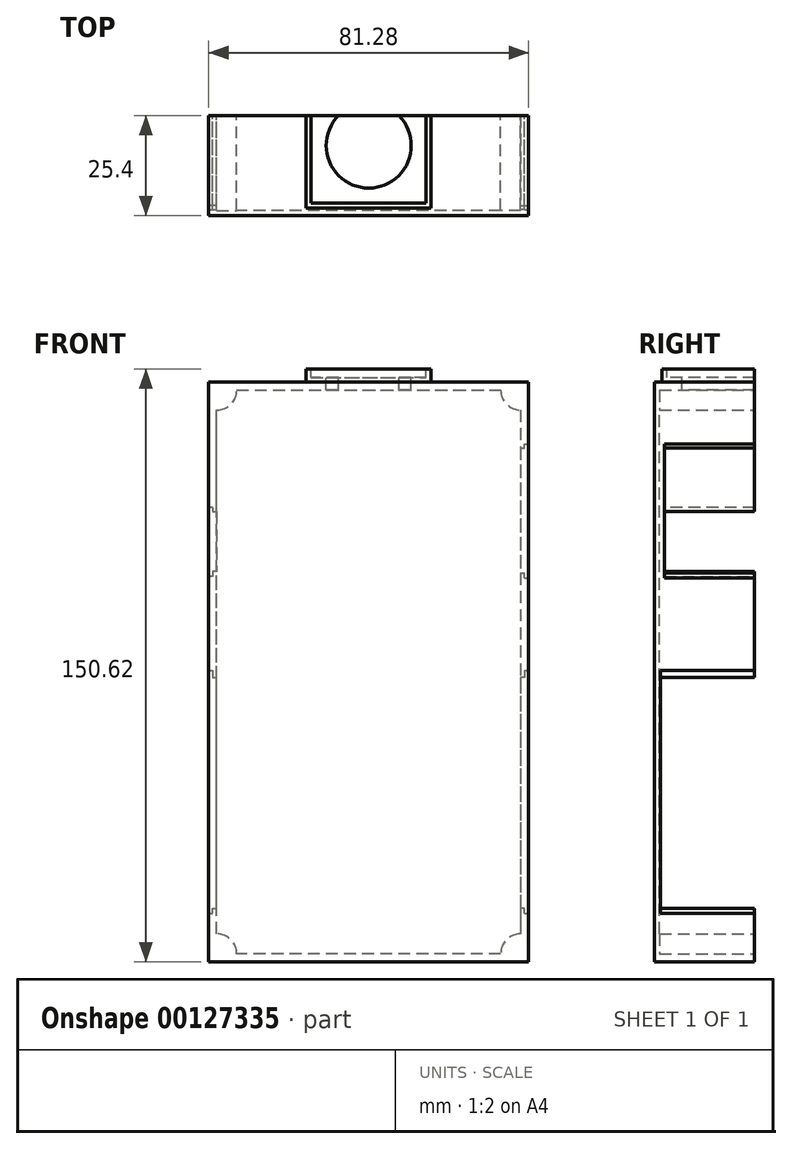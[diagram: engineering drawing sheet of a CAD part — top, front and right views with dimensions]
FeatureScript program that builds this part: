
annotation { "Feature Type Name" : "Feature", "Feature Type Description" : "" }
export const myFeature = defineFeature(function(context is Context, id is Id, definition is map)
    precondition{}
    {
        {
            var Q0;
            Q0=qCreatedBy(makeId("Front.planeOp"),FACE);
            var sketch = newSketch(context, id + "F0", { "sketchPlane" : qUnion([Q0])});
            skLineSegment(sketch, "E0", {"start": v(36.47, 73.76) * mm, "end": v(-44.81, 73.76) * mm});
            skLineSegment(sketch, "E1", {"start": v(-44.81, 73.76) * mm, "end": v(-44.81, -40.54) * mm});
            skLineSegment(sketch, "E2", {"start": v(36.47, -40.54) * mm, "end": v(36.47, 73.76) * mm});
            skLineSegment(sketch, "E3", {"start": v(36.47, -40.54) * mm, "end": v(36.47, -73.56) * mm});
            skLineSegment(sketch, "E4", {"start": v(36.47, -73.56) * mm, "end": v(-44.81, -73.56) * mm});
            skLineSegment(sketch, "E5", {"start": v(-44.81, -73.56) * mm, "end": v(-44.81, -40.54) * mm});
            skSolve(sketch);
        }
        {
            var Q0;
            Q0 = qSketchRegion(id + "F0", true);
            extrude(context, id + "F1", {"entities" : qUnion([Q0]), "depth" : 25.4 * mm});
        }
        {
            var Q0;
            Q0=makeQuery(id+"F1.opExtrude","CAP_FACE",FACE,{"disambiguationData":[OSD([sQuery(id+"F0.wireOp",EDGE,"E0"),sQuery(id+"F0.wireOp",EDGE,"E1"),sQuery(id+"F0.wireOp",EDGE,"9LGxaBVT-J4aD-Pj7p-0tie-yeeoXnwk5BCI"),sQuery(id+"F0.wireOp",EDGE,"E2")])],"isStart":true});
            var sketch = newSketch(context, id + "F2", { "sketchPlane" : qUnion([Q0])});
            skLineSegment(sketch, "E6", {"start": v(-34.44, 71.73) * mm, "end": v(-34.44, -71.53) * mm});
            skLineSegment(sketch, "E7", {"start": v(-34.44, -71.53) * mm, "end": v(42.78, -71.53) * mm});
            skLineSegment(sketch, "E8", {"start": v(42.78, -71.53) * mm, "end": v(42.78, 71.73) * mm});
            skLineSegment(sketch, "E9", {"start": v(42.78, 71.73) * mm, "end": v(-34.44, 71.73) * mm});
            skSolve(sketch);
        }
        {
            var Q0;
            Q0 = qSketchRegion(id + "F2", true);
            extrude(context, id + "F3", {"entities" : qUnion([Q0]), "operationType" : NewBodyOperationType.REMOVE, "oppositeDirection" : true, "depth" : 24.13 * mm});
        }
        {
            var Q0;
            Q0=makeQuery(id+"F1.opExtrude","SWEPT_FACE",FACE,{"disambiguationData":[OSD([sQuery(id+"F0.wireOp",EDGE,"E2")])]});
            var sketch = newSketch(context, id + "F4", { "sketchPlane" : qUnion([Q0])});
            skLineSegment(sketch, "E10", {"start": v(-25.4, 20.55) * mm, "end": v(-25.4, -0.03) * mm});
            skLineSegment(sketch, "E11", {"start": v(-13.14, -8) * mm, "end": v(-13.14, -14.85) * mm});
            skLineSegment(sketch, "E12", {"start": v(-13.14, -14.85) * mm, "end": v(-12.26, -14.85) * mm});
            skLineSegment(sketch, "E13", {"start": v(-12.26, -14.85) * mm, "end": v(-12.26, -8) * mm});
            skLineSegment(sketch, "E14", {"start": v(-12.26, -8) * mm, "end": v(-13.14, -8) * mm});
            skLineSegment(sketch, "E15", {"start": v(-16.13, -19.42) * mm, "end": v(-16.13, -20.31) * mm});
            skLineSegment(sketch, "E16", {"start": v(-16.13, -20.31) * mm, "end": v(-9.27, -20.31) * mm});
            skLineSegment(sketch, "E17", {"start": v(-9.27, -20.31) * mm, "end": v(-9.27, -19.42) * mm});
            skLineSegment(sketch, "E18", {"start": v(-9.27, -19.42) * mm, "end": v(-16.13, -19.42) * mm});
            skLineSegment(sketch, "E19", {"start": v(-16.13, -27.42) * mm, "end": v(-16.13, -28.31) * mm});
            skLineSegment(sketch, "E20", {"start": v(-16.13, -28.31) * mm, "end": v(-9.27, -28.31) * mm});
            skLineSegment(sketch, "E21", {"start": v(-9.27, -28.31) * mm, "end": v(-9.27, -27.42) * mm});
            skLineSegment(sketch, "E22", {"start": v(-9.27, -27.42) * mm, "end": v(-16.13, -27.42) * mm});
            skLineSegment(sketch, "E23", {"start": v(-21.46, -16.06) * mm, "end": v(-21.46, -22.91) * mm});
            skLineSegment(sketch, "E24", {"start": v(-21.46, -22.91) * mm, "end": v(-20.57, -22.91) * mm});
            skLineSegment(sketch, "E25", {"start": v(-20.57, -22.91) * mm, "end": v(-20.57, -16.06) * mm});
            skLineSegment(sketch, "E26", {"start": v(-20.57, -16.06) * mm, "end": v(-21.46, -16.06) * mm});
            skLineSegment(sketch, "E27", {"start": v(-4.83, -16.06) * mm, "end": v(-4.83, -22.91) * mm});
            skLineSegment(sketch, "E28", {"start": v(-4.83, -22.91) * mm, "end": v(-3.94, -22.91) * mm});
            skLineSegment(sketch, "E29", {"start": v(-3.94, -22.91) * mm, "end": v(-3.94, -16.06) * mm});
            skLineSegment(sketch, "E30", {"start": v(-3.94, -16.06) * mm, "end": v(-4.83, -16.06) * mm});
            skSolve(sketch);
        }
        {
            var Q0;
            Q0 = qSketchRegion(id + "F4", true);
            extrude(context, id + "F5", {"entities" : qUnion([Q0]), "operationType" : NewBodyOperationType.REMOVE, "endBound" : BoundingType.THROUGH_ALL, "oppositeDirection" : true, "depth" : 25.4 * mm});
        }
        {
            var Q0;
            Q0=makeQuery(id+"F1.opExtrude","SWEPT_FACE",FACE,{"disambiguationData":[OSD([sQuery(id+"F0.wireOp",EDGE,"E2")])]});
            var sketch = newSketch(context, id + "F6", { "sketchPlane" : qUnion([Q0])});
            skLineSegment(sketch, "E31", {"start": v(-25.4, 20.55) * mm, "end": v(-25.4, -0.03) * mm});
            skLineSegment(sketch, "E32", {"start": v(-19.94, 28.85) * mm, "end": v(-19.94, 28.17) * mm});
            skLineSegment(sketch, "E33", {"start": v(-19.94, 28.17) * mm, "end": v(-14.94, 28.17) * mm});
            skLineSegment(sketch, "E34", {"start": v(-14.94, 28.17) * mm, "end": v(-14.94, 28.85) * mm});
            skLineSegment(sketch, "E35", {"start": v(-14.94, 28.85) * mm, "end": v(-19.94, 28.85) * mm});
            skLineSegment(sketch, "E36", {"start": v(-10.46, 28.85) * mm, "end": v(-5.46, 28.85) * mm});
            skLineSegment(sketch, "E37", {"start": v(-5.46, 28.85) * mm, "end": v(-5.46, 28.17) * mm});
            skLineSegment(sketch, "E38", {"start": v(-5.46, 28.17) * mm, "end": v(-10.46, 28.17) * mm});
            skLineSegment(sketch, "E39", {"start": v(-10.46, 28.17) * mm, "end": v(-10.46, 28.85) * mm});
            skLineSegment(sketch, "E40", {"start": v(-19.94, 37.16) * mm, "end": v(-19.94, 36.47) * mm});
            skLineSegment(sketch, "E41", {"start": v(-19.94, 36.47) * mm, "end": v(-14.94, 36.47) * mm});
            skLineSegment(sketch, "E42", {"start": v(-14.94, 36.47) * mm, "end": v(-14.94, 37.16) * mm});
            skLineSegment(sketch, "E43", {"start": v(-14.94, 37.16) * mm, "end": v(-19.94, 37.16) * mm});
            skLineSegment(sketch, "E44", {"start": v(-10.46, 37.16) * mm, "end": v(-10.46, 36.47) * mm});
            skLineSegment(sketch, "E45", {"start": v(-10.46, 36.47) * mm, "end": v(-5.46, 36.47) * mm});
            skLineSegment(sketch, "E46", {"start": v(-5.46, 36.47) * mm, "end": v(-5.46, 37.16) * mm});
            skLineSegment(sketch, "E47", {"start": v(-5.46, 37.16) * mm, "end": v(-10.46, 37.16) * mm});
            skLineSegment(sketch, "E48", {"start": v(-19.94, 45.46) * mm, "end": v(-19.94, 44.78) * mm});
            skLineSegment(sketch, "E49", {"start": v(-19.94, 44.78) * mm, "end": v(-14.94, 44.78) * mm});
            skLineSegment(sketch, "E50", {"start": v(-14.94, 44.78) * mm, "end": v(-14.94, 45.46) * mm});
            skLineSegment(sketch, "E51", {"start": v(-14.94, 45.46) * mm, "end": v(-19.94, 45.46) * mm});
            skLineSegment(sketch, "E52", {"start": v(-10.46, 45.46) * mm, "end": v(-10.46, 44.78) * mm});
            skLineSegment(sketch, "E53", {"start": v(-10.46, 44.78) * mm, "end": v(-5.46, 44.78) * mm});
            skLineSegment(sketch, "E54", {"start": v(-5.46, 44.78) * mm, "end": v(-5.46, 45.46) * mm});
            skLineSegment(sketch, "E55", {"start": v(-5.46, 45.46) * mm, "end": v(-10.46, 45.46) * mm});
            skLineSegment(sketch, "E56", {"start": v(-19.94, 53.77) * mm, "end": v(-19.94, 53.08) * mm});
            skLineSegment(sketch, "E57", {"start": v(-19.94, 53.08) * mm, "end": v(-14.94, 53.08) * mm});
            skLineSegment(sketch, "E58", {"start": v(-14.94, 53.08) * mm, "end": v(-14.94, 53.77) * mm});
            skLineSegment(sketch, "E59", {"start": v(-14.94, 53.77) * mm, "end": v(-19.94, 53.77) * mm});
            skLineSegment(sketch, "E60", {"start": v(-10.46, 53.77) * mm, "end": v(-10.46, 53.08) * mm});
            skLineSegment(sketch, "E61", {"start": v(-10.46, 53.08) * mm, "end": v(-5.46, 53.08) * mm});
            skLineSegment(sketch, "E62", {"start": v(-5.46, 53.08) * mm, "end": v(-5.46, 53.77) * mm});
            skLineSegment(sketch, "E63", {"start": v(-5.46, 53.77) * mm, "end": v(-10.46, 53.77) * mm});
            skSolve(sketch);
        }
        {
            var Q0;
            Q0 = qSketchRegion(id + "F6", true);
            extrude(context, id + "F7", {"entities" : qUnion([Q0]), "operationType" : NewBodyOperationType.REMOVE, "endBound" : BoundingType.THROUGH_ALL, "oppositeDirection" : true, "depth" : 25.4 * mm});
        }
        {
            var Q0;
            Q0=makeQuery(id+"F1.opExtrude","SWEPT_FACE",FACE,{"disambiguationData":[OSD([sQuery(id+"F0.wireOp",EDGE,"E1")])]});
            var sketch = newSketch(context, id + "F8", { "sketchPlane" : qUnion([Q0])});
            skLineSegment(sketch, "E64", {"start": v(5.46, 53.77) * mm, "end": v(5.46, 53.08) * mm});
            skLineSegment(sketch, "E65", {"start": v(5.46, 53.08) * mm, "end": v(10.46, 53.08) * mm});
            skLineSegment(sketch, "E66", {"start": v(10.46, 53.08) * mm, "end": v(10.46, 53.77) * mm});
            skLineSegment(sketch, "E67", {"start": v(10.46, 53.77) * mm, "end": v(5.46, 53.77) * mm});
            skLineSegment(sketch, "E68", {"start": v(14.94, 53.77) * mm, "end": v(14.94, 53.08) * mm});
            skLineSegment(sketch, "E69", {"start": v(14.94, 53.08) * mm, "end": v(19.94, 53.08) * mm});
            skLineSegment(sketch, "E70", {"start": v(19.94, 53.08) * mm, "end": v(19.94, 53.77) * mm});
            skLineSegment(sketch, "E71", {"start": v(19.94, 53.77) * mm, "end": v(14.94, 53.77) * mm});
            skLineSegment(sketch, "E72", {"start": v(5.46, 45.46) * mm, "end": v(5.46, 44.78) * mm});
            skLineSegment(sketch, "E73", {"start": v(5.46, 44.78) * mm, "end": v(10.46, 44.78) * mm});
            skLineSegment(sketch, "E74", {"start": v(10.46, 44.78) * mm, "end": v(10.46, 45.46) * mm});
            skLineSegment(sketch, "E75", {"start": v(10.46, 45.46) * mm, "end": v(5.46, 45.46) * mm});
            skLineSegment(sketch, "E76", {"start": v(14.94, 45.46) * mm, "end": v(14.94, 44.78) * mm});
            skLineSegment(sketch, "E77", {"start": v(14.94, 44.78) * mm, "end": v(19.94, 44.78) * mm});
            skLineSegment(sketch, "E78", {"start": v(19.94, 44.78) * mm, "end": v(19.94, 45.46) * mm});
            skLineSegment(sketch, "E79", {"start": v(19.94, 45.46) * mm, "end": v(14.94, 45.46) * mm});
            skSolve(sketch);
        }
        {
            var Q0;
            Q0 = qSketchRegion(id + "F8", true);
            extrude(context, id + "F9", {"entities" : qUnion([Q0]), "operationType" : NewBodyOperationType.ADD, "oppositeDirection" : true, "depth" : 2.03 * mm});
        }
        {
            var Q0;
            Q0=makeQuery(id+"F1.opExtrude","SWEPT_FACE",FACE,{"disambiguationData":[OSD([sQuery(id+"F0.wireOp",EDGE,"E2")])]});
            var sketch = newSketch(context, id + "F10", { "sketchPlane" : qUnion([Q0])});
            skLineSegment(sketch, "E80", {"start": v(-19.43, -15.67) * mm, "end": v(-22.6, -15.67) * mm});
            skLineSegment(sketch, "E81", {"start": v(-22.6, -15.67) * mm, "end": v(-22.6, -23.3) * mm});
            skLineSegment(sketch, "E82", {"start": v(-22.6, -23.3) * mm, "end": v(-19.43, -23.3) * mm});
            skLineSegment(sketch, "E83", {"start": v(-19.43, -23.3) * mm, "end": v(-19.43, -15.67) * mm});
            skLineSegment(sketch, "E84", {"start": v(-16.51, -18.28) * mm, "end": v(-16.51, -21.45) * mm});
            skLineSegment(sketch, "E85", {"start": v(-16.51, -21.45) * mm, "end": v(-8.9, -21.45) * mm});
            skLineSegment(sketch, "E86", {"start": v(-8.9, -21.45) * mm, "end": v(-8.9, -18.28) * mm});
            skLineSegment(sketch, "E87", {"start": v(-8.9, -18.28) * mm, "end": v(-16.51, -18.28) * mm});
            skLineSegment(sketch, "E88", {"start": v(-2.8, -15.67) * mm, "end": v(-5.97, -15.67) * mm});
            skLineSegment(sketch, "E89", {"start": v(-5.97, -15.67) * mm, "end": v(-5.97, -23.3) * mm});
            skLineSegment(sketch, "E90", {"start": v(-5.97, -23.3) * mm, "end": v(-2.8, -23.3) * mm});
            skLineSegment(sketch, "E91", {"start": v(-2.8, -23.3) * mm, "end": v(-2.8, -15.67) * mm});
            skLineSegment(sketch, "E92", {"start": v(-11.11, -7.61) * mm, "end": v(-14.29, -7.61) * mm});
            skLineSegment(sketch, "E93", {"start": v(-14.29, -7.61) * mm, "end": v(-14.29, -15.23) * mm});
            skLineSegment(sketch, "E94", {"start": v(-14.29, -15.23) * mm, "end": v(-11.11, -15.23) * mm});
            skLineSegment(sketch, "E95", {"start": v(-11.11, -15.23) * mm, "end": v(-11.11, -7.61) * mm});
            skLineSegment(sketch, "E96", {"start": v(-16.5, -26.28) * mm, "end": v(-16.5, -29.45) * mm});
            skLineSegment(sketch, "E97", {"start": v(-16.5, -29.45) * mm, "end": v(-8.89, -29.45) * mm});
            skLineSegment(sketch, "E98", {"start": v(-8.89, -29.45) * mm, "end": v(-8.89, -26.28) * mm});
            skLineSegment(sketch, "E99", {"start": v(-8.89, -26.28) * mm, "end": v(-16.5, -26.28) * mm});
            skLineSegment(sketch, "E100", {"start": v(-10.1, -6.6) * mm, "end": v(-15.3, -6.6) * mm});
            skLineSegment(sketch, "E101", {"start": v(-15.3, -6.6) * mm, "end": v(-15.3, -16.25) * mm});
            skLineSegment(sketch, "E102", {"start": v(-15.3, -16.25) * mm, "end": v(-10.1, -16.25) * mm});
            skLineSegment(sketch, "E103", {"start": v(-10.1, -16.25) * mm, "end": v(-10.1, -6.6) * mm});
            skLineSegment(sketch, "E104", {"start": v(-23.62, -14.66) * mm, "end": v(-23.62, -24.31) * mm});
            skLineSegment(sketch, "E105", {"start": v(-23.62, -24.31) * mm, "end": v(-18.41, -24.31) * mm});
            skLineSegment(sketch, "E106", {"start": v(-18.42, -24.31) * mm, "end": v(-18.42, -14.66) * mm});
            skLineSegment(sketch, "E107", {"start": v(-18.42, -14.66) * mm, "end": v(-23.62, -14.66) * mm});
            skLineSegment(sketch, "E108", {"start": v(-1.78, -14.66) * mm, "end": v(-6.98, -14.66) * mm});
            skLineSegment(sketch, "E109", {"start": v(-6.98, -14.66) * mm, "end": v(-6.98, -24.31) * mm});
            skLineSegment(sketch, "E110", {"start": v(-6.98, -24.31) * mm, "end": v(-1.78, -24.31) * mm});
            skLineSegment(sketch, "E111", {"start": v(-1.78, -24.31) * mm, "end": v(-1.78, -14.66) * mm});
            skLineSegment(sketch, "E112", {"start": v(-17.53, -17.26) * mm, "end": v(-17.53, -22.47) * mm});
            skLineSegment(sketch, "E113", {"start": v(-17.53, -22.47) * mm, "end": v(-7.87, -22.47) * mm});
            skLineSegment(sketch, "E114", {"start": v(-7.87, -22.47) * mm, "end": v(-7.87, -17.26) * mm});
            skLineSegment(sketch, "E115", {"start": v(-7.87, -17.26) * mm, "end": v(-17.53, -17.26) * mm});
            skLineSegment(sketch, "E116", {"start": v(-17.53, -25.26) * mm, "end": v(-17.53, -30.47) * mm});
            skLineSegment(sketch, "E117", {"start": v(-17.53, -30.47) * mm, "end": v(-8.25, -30.47) * mm});
            skLineSegment(sketch, "E118", {"start": v(-8.25, -30.47) * mm, "end": v(-8.25, -25.26) * mm});
            skLineSegment(sketch, "E119", {"start": v(-8.25, -25.26) * mm, "end": v(-17.53, -25.26) * mm});
            skSolve(sketch);
        }
        {
            var Q0;
            Q0 = qSketchRegion(id + "F10", true);
            extrude(context, id + "F11", {"entities" : qUnion([Q0]), "operationType" : NewBodyOperationType.ADD, "oppositeDirection" : true, "depth" : 12.95 * mm});
        }
        {
            var Q0;
            Q0=makeQuery(id+"F1.opExtrude","SWEPT_FACE",FACE,{"disambiguationData":[OSD([sQuery(id+"F0.wireOp",EDGE,"E2")])]});
            var sketch = newSketch(context, id + "F12", { "sketchPlane" : qUnion([Q0])});
            skLineSegment(sketch, "E120", {"start": v(-21.25, 30.1) * mm, "end": v(-21.25, 26.92) * mm});
            skLineSegment(sketch, "E121", {"start": v(-21.25, 26.92) * mm, "end": v(-13.63, 26.92) * mm});
            skLineSegment(sketch, "E122", {"start": v(-13.63, 26.92) * mm, "end": v(-13.63, 30.1) * mm});
            skLineSegment(sketch, "E123", {"start": v(-13.63, 30.1) * mm, "end": v(-21.25, 30.1) * mm});
            skLineSegment(sketch, "E124", {"start": v(-22, 30.86) * mm, "end": v(-22, 26.16) * mm});
            skLineSegment(sketch, "E125", {"start": v(-22, 26.16) * mm, "end": v(-12.87, 26.16) * mm});
            skLineSegment(sketch, "E126", {"start": v(-12.87, 26.16) * mm, "end": v(-12.87, 30.86) * mm});
            skLineSegment(sketch, "E127", {"start": v(-12.87, 30.86) * mm, "end": v(-22, 30.86) * mm});
            skLineSegment(sketch, "E128", {"start": v(-11.77, 30.1) * mm, "end": v(-11.77, 26.92) * mm});
            skLineSegment(sketch, "E129", {"start": v(-11.77, 26.92) * mm, "end": v(-4.15, 26.92) * mm});
            skLineSegment(sketch, "E130", {"start": v(-4.15, 26.92) * mm, "end": v(-4.15, 30.1) * mm});
            skLineSegment(sketch, "E131", {"start": v(-4.15, 30.1) * mm, "end": v(-11.77, 30.1) * mm});
            skLineSegment(sketch, "E132", {"start": v(-3.4, 30.86) * mm, "end": v(-12.53, 30.86) * mm});
            skLineSegment(sketch, "E133", {"start": v(-12.53, 30.86) * mm, "end": v(-12.53, 26.16) * mm});
            skLineSegment(sketch, "E134", {"start": v(-12.53, 26.16) * mm, "end": v(-3.4, 26.16) * mm});
            skLineSegment(sketch, "E135", {"start": v(-3.4, 26.16) * mm, "end": v(-3.4, 30.86) * mm});
            skLineSegment(sketch, "E136", {"start": v(-21.25, 38.4) * mm, "end": v(-21.25, 35.23) * mm});
            skLineSegment(sketch, "E137", {"start": v(-21.25, 35.23) * mm, "end": v(-13.63, 35.23) * mm});
            skLineSegment(sketch, "E138", {"start": v(-13.63, 35.23) * mm, "end": v(-13.63, 38.4) * mm});
            skLineSegment(sketch, "E139", {"start": v(-13.63, 38.4) * mm, "end": v(-21.25, 38.4) * mm});
            skLineSegment(sketch, "E140", {"start": v(-22, 39.17) * mm, "end": v(-22, 34.47) * mm});
            skLineSegment(sketch, "E141", {"start": v(-22, 34.47) * mm, "end": v(-12.87, 34.47) * mm});
            skLineSegment(sketch, "E142", {"start": v(-12.87, 34.47) * mm, "end": v(-12.87, 39.17) * mm});
            skLineSegment(sketch, "E143", {"start": v(-12.87, 39.17) * mm, "end": v(-22, 39.17) * mm});
            skLineSegment(sketch, "E144", {"start": v(-11.77, 38.4) * mm, "end": v(-11.77, 35.23) * mm});
            skLineSegment(sketch, "E145", {"start": v(-11.77, 35.23) * mm, "end": v(-4.15, 35.23) * mm});
            skLineSegment(sketch, "E146", {"start": v(-4.15, 35.23) * mm, "end": v(-4.15, 38.4) * mm});
            skLineSegment(sketch, "E147", {"start": v(-4.15, 38.4) * mm, "end": v(-11.77, 38.4) * mm});
            skLineSegment(sketch, "E148", {"start": v(-12.53, 39.17) * mm, "end": v(-12.53, 34.47) * mm});
            skLineSegment(sketch, "E149", {"start": v(-12.53, 39.17) * mm, "end": v(-3.4, 39.17) * mm});
            skLineSegment(sketch, "E150", {"start": v(-3.4, 39.17) * mm, "end": v(-3.4, 34.47) * mm});
            skLineSegment(sketch, "E151", {"start": v(-3.4, 34.47) * mm, "end": v(-12.53, 34.47) * mm});
            skLineSegment(sketch, "E152", {"start": v(-21.25, 46.7) * mm, "end": v(-21.25, 43.53) * mm});
            skLineSegment(sketch, "E153", {"start": v(-21.25, 43.53) * mm, "end": v(-13.63, 43.53) * mm});
            skLineSegment(sketch, "E154", {"start": v(-13.63, 43.53) * mm, "end": v(-13.63, 46.7) * mm});
            skLineSegment(sketch, "E155", {"start": v(-13.63, 46.7) * mm, "end": v(-21.25, 46.7) * mm});
            skLineSegment(sketch, "E156", {"start": v(-22, 47.47) * mm, "end": v(-22, 42.77) * mm});
            skLineSegment(sketch, "E157", {"start": v(-22, 42.77) * mm, "end": v(-12.87, 42.77) * mm});
            skLineSegment(sketch, "E158", {"start": v(-12.87, 42.77) * mm, "end": v(-12.87, 47.47) * mm});
            skLineSegment(sketch, "E159", {"start": v(-12.87, 47.47) * mm, "end": v(-22, 47.47) * mm});
            skLineSegment(sketch, "E160", {"start": v(-11.77, 43.53) * mm, "end": v(-4.15, 43.53) * mm});
            skLineSegment(sketch, "E161", {"start": v(-4.15, 46.7) * mm, "end": v(-11.77, 46.7) * mm});
            skLineSegment(sketch, "E162", {"start": v(-11.77, 46.7) * mm, "end": v(-11.77, 43.53) * mm});
            skLineSegment(sketch, "E163", {"start": v(-4.15, 46.7) * mm, "end": v(-4.15, 43.53) * mm});
            skLineSegment(sketch, "E164", {"start": v(-12.53, 47.47) * mm, "end": v(-12.53, 42.77) * mm});
            skLineSegment(sketch, "E165", {"start": v(-12.53, 42.77) * mm, "end": v(-3.4, 42.77) * mm});
            skLineSegment(sketch, "E166", {"start": v(-3.4, 42.77) * mm, "end": v(-3.4, 47.47) * mm});
            skLineSegment(sketch, "E167", {"start": v(-3.4, 47.47) * mm, "end": v(-12.53, 47.47) * mm});
            skLineSegment(sketch, "E168", {"start": v(-21.25, 55.01) * mm, "end": v(-21.25, 51.84) * mm});
            skLineSegment(sketch, "E169", {"start": v(-21.25, 51.84) * mm, "end": v(-13.63, 51.84) * mm});
            skLineSegment(sketch, "E170", {"start": v(-13.63, 51.84) * mm, "end": v(-13.63, 55.01) * mm});
            skLineSegment(sketch, "E171", {"start": v(-13.63, 55.01) * mm, "end": v(-21.25, 55.01) * mm});
            skLineSegment(sketch, "E172", {"start": v(-11.77, 55.01) * mm, "end": v(-11.77, 51.84) * mm});
            skLineSegment(sketch, "E173", {"start": v(-11.77, 51.84) * mm, "end": v(-4.15, 51.84) * mm});
            skLineSegment(sketch, "E174", {"start": v(-4.15, 51.84) * mm, "end": v(-4.15, 55.01) * mm});
            skLineSegment(sketch, "E175", {"start": v(-4.15, 55.01) * mm, "end": v(-11.77, 55.01) * mm});
            skLineSegment(sketch, "E176", {"start": v(-22, 55.78) * mm, "end": v(-22, 51.08) * mm});
            skLineSegment(sketch, "E177", {"start": v(-22, 51.08) * mm, "end": v(-12.87, 51.08) * mm});
            skLineSegment(sketch, "E178", {"start": v(-12.87, 51.08) * mm, "end": v(-12.87, 55.78) * mm});
            skLineSegment(sketch, "E179", {"start": v(-12.87, 55.78) * mm, "end": v(-22, 55.78) * mm});
            skLineSegment(sketch, "E180", {"start": v(-12.53, 55.78) * mm, "end": v(-12.53, 51.08) * mm});
            skLineSegment(sketch, "E181", {"start": v(-12.53, 51.08) * mm, "end": v(-3.4, 51.08) * mm});
            skLineSegment(sketch, "E182", {"start": v(-3.4, 51.08) * mm, "end": v(-3.4, 55.78) * mm});
            skLineSegment(sketch, "E183", {"start": v(-3.4, 55.78) * mm, "end": v(-12.53, 55.78) * mm});
            skSolve(sketch);
        }
        {
            var Q0;
            Q0 = qSketchRegion(id + "F12", true);
            extrude(context, id + "F13", {"entities" : qUnion([Q0]), "operationType" : NewBodyOperationType.ADD, "oppositeDirection" : true, "depth" : 12.95 * mm});
        }
        {
            var Q0;
            Q0=makeQuery(id+"F1.opExtrude","SWEPT_FACE",FACE,{"disambiguationData":[OSD([sQuery(id+"F0.wireOp",EDGE,"E2"),sQuery(id+"F0.wireOp",EDGE,"E3")])]});
            var sketch = newSketch(context, id + "F14", { "sketchPlane" : qUnion([Q0])});
            skLineSegment(sketch, "E184", {"start": v(-13.14, -37.16) * mm, "end": v(-12.26, -37.16) * mm});
            skLineSegment(sketch, "E185", {"start": v(-13.14, -37.16) * mm, "end": v(-13.14, -44.02) * mm});
            skLineSegment(sketch, "E186", {"start": v(-13.14, -44.02) * mm, "end": v(-12.26, -44.02) * mm});
            skLineSegment(sketch, "E187", {"start": v(-12.26, -44.02) * mm, "end": v(-12.26, -37.16) * mm});
            skLineSegment(sketch, "E188", {"start": v(-16.13, -48.59) * mm, "end": v(-16.13, -49.48) * mm});
            skLineSegment(sketch, "E189", {"start": v(-16.13, -49.48) * mm, "end": v(-9.27, -49.48) * mm});
            skLineSegment(sketch, "E190", {"start": v(-9.27, -49.48) * mm, "end": v(-9.27, -48.59) * mm});
            skLineSegment(sketch, "E191", {"start": v(-9.27, -48.59) * mm, "end": v(-16.13, -48.59) * mm});
            skLineSegment(sketch, "E192", {"start": v(-16.13, -56.59) * mm, "end": v(-16.13, -57.48) * mm});
            skLineSegment(sketch, "E193", {"start": v(-16.13, -57.48) * mm, "end": v(-9.27, -57.48) * mm});
            skLineSegment(sketch, "E194", {"start": v(-9.27, -57.48) * mm, "end": v(-9.27, -56.59) * mm});
            skLineSegment(sketch, "E195", {"start": v(-9.27, -56.59) * mm, "end": v(-16.13, -56.59) * mm});
            skLineSegment(sketch, "E196", {"start": v(-21.46, -45.29) * mm, "end": v(-21.46, -52.14) * mm});
            skLineSegment(sketch, "E197", {"start": v(-21.46, -52.14) * mm, "end": v(-20.57, -52.14) * mm});
            skLineSegment(sketch, "E198", {"start": v(-20.57, -52.14) * mm, "end": v(-20.57, -45.29) * mm});
            skLineSegment(sketch, "E199", {"start": v(-20.57, -45.29) * mm, "end": v(-21.46, -45.29) * mm});
            skLineSegment(sketch, "E200", {"start": v(-4.83, -45.29) * mm, "end": v(-4.83, -52.14) * mm});
            skLineSegment(sketch, "E201", {"start": v(-4.83, -52.14) * mm, "end": v(-3.94, -52.14) * mm});
            skLineSegment(sketch, "E202", {"start": v(-3.94, -52.14) * mm, "end": v(-3.94, -45.29) * mm});
            skLineSegment(sketch, "E203", {"start": v(-3.94, -45.29) * mm, "end": v(-4.83, -45.29) * mm});
            skSolve(sketch);
        }
        {
            var Q0;
            Q0 = qSketchRegion(id + "F14", true);
            extrude(context, id + "F15", {"entities" : qUnion([Q0]), "operationType" : NewBodyOperationType.REMOVE, "endBound" : BoundingType.THROUGH_ALL, "oppositeDirection" : true, "depth" : 25.4 * mm});
        }
        {
            var Q0;
            Q0=makeQuery(id+"F9.boolean.opBoolean","MERGE",FACE,{"derivedFrom":[makeQuery(id+"F1.opExtrude","SWEPT_FACE",FACE,{"disambiguationData":[OSD([sQuery(id+"F0.wireOp",EDGE,"E1"),sQuery(id+"F0.wireOp",EDGE,"E5")])]}),makeQuery(id+"F9.opExtrude","CAP_FACE",FACE,{"disambiguationData":[OSD([sQuery(id+"F8.wireOp",EDGE,"E64"),sQuery(id+"F8.wireOp",EDGE,"E65"),sQuery(id+"F8.wireOp",EDGE,"E66"),sQuery(id+"F8.wireOp",EDGE,"E67")])],"isStart":true}),makeQuery(id+"F9.opExtrude","CAP_FACE",FACE,{"disambiguationData":[OSD([sQuery(id+"F8.wireOp",EDGE,"E68"),sQuery(id+"F8.wireOp",EDGE,"E69"),sQuery(id+"F8.wireOp",EDGE,"E70"),sQuery(id+"F8.wireOp",EDGE,"E71")])],"isStart":true}),makeQuery(id+"F9.opExtrude","CAP_FACE",FACE,{"disambiguationData":[OSD([sQuery(id+"F8.wireOp",EDGE,"E72"),sQuery(id+"F8.wireOp",EDGE,"E73"),sQuery(id+"F8.wireOp",EDGE,"E74"),sQuery(id+"F8.wireOp",EDGE,"E75")])],"isStart":true}),makeQuery(id+"F9.opExtrude","CAP_FACE",FACE,{"disambiguationData":[OSD([sQuery(id+"F8.wireOp",EDGE,"E76"),sQuery(id+"F8.wireOp",EDGE,"E77"),sQuery(id+"F8.wireOp",EDGE,"E78"),sQuery(id+"F8.wireOp",EDGE,"E79")])],"isStart":true})]});
            var sketch = newSketch(context, id + "F16", { "sketchPlane" : qUnion([Q0])});
            skLineSegment(sketch, "E204", {"start": v(11.11, -7.61) * mm, "end": v(11.11, -15.23) * mm});
            skLineSegment(sketch, "E205", {"start": v(11.11, -15.23) * mm, "end": v(14.29, -15.23) * mm});
            skLineSegment(sketch, "E206", {"start": v(14.29, -15.23) * mm, "end": v(14.29, -7.61) * mm});
            skLineSegment(sketch, "E207", {"start": v(14.29, -7.61) * mm, "end": v(11.11, -7.61) * mm});
            skLineSegment(sketch, "E208", {"start": v(5.97, -15.67) * mm, "end": v(2.8, -15.67) * mm});
            skLineSegment(sketch, "E209", {"start": v(2.8, -15.67) * mm, "end": v(2.8, -23.3) * mm});
            skLineSegment(sketch, "E210", {"start": v(2.8, -23.3) * mm, "end": v(5.97, -23.3) * mm});
            skLineSegment(sketch, "E211", {"start": v(5.97, -23.3) * mm, "end": v(5.97, -15.67) * mm});
            skLineSegment(sketch, "E212", {"start": v(8.9, -18.28) * mm, "end": v(8.9, -21.45) * mm});
            skLineSegment(sketch, "E213", {"start": v(8.9, -21.45) * mm, "end": v(16.51, -21.45) * mm});
            skLineSegment(sketch, "E214", {"start": v(16.51, -21.45) * mm, "end": v(16.51, -18.28) * mm});
            skLineSegment(sketch, "E215", {"start": v(16.51, -18.28) * mm, "end": v(8.9, -18.28) * mm});
            skLineSegment(sketch, "E216", {"start": v(19.43, -15.67) * mm, "end": v(19.43, -23.3) * mm});
            skLineSegment(sketch, "E217", {"start": v(19.43, -23.3) * mm, "end": v(22.6, -23.3) * mm});
            skLineSegment(sketch, "E218", {"start": v(22.6, -23.3) * mm, "end": v(22.6, -15.67) * mm});
            skLineSegment(sketch, "E219", {"start": v(22.6, -15.67) * mm, "end": v(19.43, -15.67) * mm});
            skLineSegment(sketch, "E220", {"start": v(8.89, -26.28) * mm, "end": v(8.89, -29.45) * mm});
            skLineSegment(sketch, "E221", {"start": v(8.89, -29.45) * mm, "end": v(16.5, -29.45) * mm});
            skLineSegment(sketch, "E222", {"start": v(16.51, -29.45) * mm, "end": v(16.51, -26.28) * mm});
            skLineSegment(sketch, "E223", {"start": v(16.5, -26.28) * mm, "end": v(8.89, -26.28) * mm});
            skLineSegment(sketch, "E224", {"start": v(6.98, -14.66) * mm, "end": v(1.78, -14.66) * mm});
            skLineSegment(sketch, "E225", {"start": v(1.78, -14.66) * mm, "end": v(1.78, -24.31) * mm});
            skLineSegment(sketch, "E226", {"start": v(1.78, -24.31) * mm, "end": v(6.98, -24.31) * mm});
            skLineSegment(sketch, "E227", {"start": v(6.98, -24.31) * mm, "end": v(6.98, -14.66) * mm});
            skLineSegment(sketch, "E228", {"start": v(7.87, -17.26) * mm, "end": v(7.87, -22.47) * mm});
            skLineSegment(sketch, "E229", {"start": v(7.87, -22.47) * mm, "end": v(17.53, -22.47) * mm});
            skLineSegment(sketch, "E230", {"start": v(17.53, -22.47) * mm, "end": v(17.53, -17.26) * mm});
            skLineSegment(sketch, "E231", {"start": v(17.53, -17.26) * mm, "end": v(7.87, -17.26) * mm});
            skLineSegment(sketch, "E232", {"start": v(18.42, -14.66) * mm, "end": v(18.42, -24.31) * mm});
            skLineSegment(sketch, "E233", {"start": v(18.42, -24.31) * mm, "end": v(23.62, -24.31) * mm});
            skLineSegment(sketch, "E234", {"start": v(23.62, -24.31) * mm, "end": v(23.62, -14.66) * mm});
            skLineSegment(sketch, "E235", {"start": v(23.62, -14.66) * mm, "end": v(18.42, -14.66) * mm});
            skLineSegment(sketch, "E236", {"start": v(10.1, -6.6) * mm, "end": v(10.1, -16.25) * mm});
            skLineSegment(sketch, "E237", {"start": v(10.1, -16.25) * mm, "end": v(15.3, -16.25) * mm});
            skLineSegment(sketch, "E238", {"start": v(15.3, -16.25) * mm, "end": v(15.3, -6.6) * mm});
            skLineSegment(sketch, "E239", {"start": v(15.3, -6.6) * mm, "end": v(10.1, -6.6) * mm});
            skLineSegment(sketch, "E240", {"start": v(7.87, -25.26) * mm, "end": v(7.87, -30.47) * mm});
            skLineSegment(sketch, "E241", {"start": v(7.87, -30.47) * mm, "end": v(17.53, -30.47) * mm});
            skLineSegment(sketch, "E242", {"start": v(17.53, -30.47) * mm, "end": v(17.53, -25.26) * mm});
            skLineSegment(sketch, "E243", {"start": v(17.53, -25.26) * mm, "end": v(7.87, -25.26) * mm});
            skLineSegment(sketch, "E244", {"start": v(14.29, -36.78) * mm, "end": v(11.11, -36.78) * mm});
            skLineSegment(sketch, "E245", {"start": v(11.11, -36.78) * mm, "end": v(11.11, -44.4) * mm});
            skLineSegment(sketch, "E246", {"start": v(11.11, -44.4) * mm, "end": v(14.29, -44.4) * mm});
            skLineSegment(sketch, "E247", {"start": v(14.29, -44.4) * mm, "end": v(14.29, -36.78) * mm});
            skLineSegment(sketch, "E248", {"start": v(5.97, -44.9) * mm, "end": v(2.8, -44.9) * mm});
            skLineSegment(sketch, "E249", {"start": v(2.8, -44.9) * mm, "end": v(2.8, -52.52) * mm});
            skLineSegment(sketch, "E250", {"start": v(2.8, -52.52) * mm, "end": v(5.97, -52.52) * mm});
            skLineSegment(sketch, "E251", {"start": v(5.97, -52.52) * mm, "end": v(5.97, -44.9) * mm});
            skLineSegment(sketch, "E252", {"start": v(8.9, -47.44) * mm, "end": v(8.9, -50.62) * mm});
            skLineSegment(sketch, "E253", {"start": v(8.9, -50.62) * mm, "end": v(16.51, -50.62) * mm});
            skLineSegment(sketch, "E254", {"start": v(16.51, -50.62) * mm, "end": v(16.51, -47.44) * mm});
            skLineSegment(sketch, "E255", {"start": v(16.51, -47.44) * mm, "end": v(8.9, -47.44) * mm});
            skLineSegment(sketch, "E256", {"start": v(19.43, -44.9) * mm, "end": v(19.43, -52.52) * mm});
            skLineSegment(sketch, "E257", {"start": v(19.43, -52.52) * mm, "end": v(22.6, -52.52) * mm});
            skLineSegment(sketch, "E258", {"start": v(22.6, -52.52) * mm, "end": v(22.6, -44.9) * mm});
            skLineSegment(sketch, "E259", {"start": v(22.6, -44.9) * mm, "end": v(19.43, -44.9) * mm});
            skLineSegment(sketch, "E260", {"start": v(8.89, -55.45) * mm, "end": v(8.89, -58.62) * mm});
            skLineSegment(sketch, "E261", {"start": v(8.89, -58.62) * mm, "end": v(16.5, -58.62) * mm});
            skLineSegment(sketch, "E262", {"start": v(16.51, -58.62) * mm, "end": v(16.51, -55.45) * mm});
            skLineSegment(sketch, "E263", {"start": v(16.5, -55.45) * mm, "end": v(8.89, -55.45) * mm});
            skLineSegment(sketch, "E264", {"start": v(6.99, -43.89) * mm, "end": v(1.78, -43.89) * mm});
            skLineSegment(sketch, "E265", {"start": v(1.78, -43.89) * mm, "end": v(1.78, -53.54) * mm});
            skLineSegment(sketch, "E266", {"start": v(1.78, -53.54) * mm, "end": v(6.99, -53.54) * mm});
            skLineSegment(sketch, "E267", {"start": v(6.99, -53.54) * mm, "end": v(6.99, -43.89) * mm});
            skLineSegment(sketch, "E268", {"start": v(7.87, -46.43) * mm, "end": v(7.87, -51.64) * mm});
            skLineSegment(sketch, "E269", {"start": v(7.87, -51.64) * mm, "end": v(17.53, -51.64) * mm});
            skLineSegment(sketch, "E270", {"start": v(17.53, -51.64) * mm, "end": v(17.53, -46.43) * mm});
            skLineSegment(sketch, "E271", {"start": v(17.53, -46.43) * mm, "end": v(7.87, -46.43) * mm});
            skLineSegment(sketch, "E272", {"start": v(18.42, -43.89) * mm, "end": v(18.41, -53.54) * mm});
            skLineSegment(sketch, "E273", {"start": v(18.41, -53.54) * mm, "end": v(23.62, -53.54) * mm});
            skLineSegment(sketch, "E274", {"start": v(23.62, -53.54) * mm, "end": v(23.62, -43.89) * mm});
            skLineSegment(sketch, "E275", {"start": v(23.62, -43.89) * mm, "end": v(18.42, -43.89) * mm});
            skLineSegment(sketch, "E276", {"start": v(10.1, -35.76) * mm, "end": v(10.1, -45.41) * mm});
            skLineSegment(sketch, "E277", {"start": v(10.1, -45.41) * mm, "end": v(15.3, -45.41) * mm});
            skLineSegment(sketch, "E278", {"start": v(15.3, -45.41) * mm, "end": v(15.3, -35.76) * mm});
            skLineSegment(sketch, "E279", {"start": v(15.3, -35.76) * mm, "end": v(10.1, -35.76) * mm});
            skLineSegment(sketch, "E280", {"start": v(7.87, -54.43) * mm, "end": v(7.87, -59.64) * mm});
            skLineSegment(sketch, "E281", {"start": v(7.87, -59.64) * mm, "end": v(17.53, -59.64) * mm});
            skLineSegment(sketch, "E282", {"start": v(17.53, -59.64) * mm, "end": v(17.53, -54.43) * mm});
            skLineSegment(sketch, "E283", {"start": v(17.53, -54.43) * mm, "end": v(7.87, -54.43) * mm});
            skSolve(sketch);
        }
        {
            var Q0;
            Q0 = qSketchRegion(id + "F16", true);
            extrude(context, id + "F17", {"entities" : qUnion([Q0]), "operationType" : NewBodyOperationType.ADD, "oppositeDirection" : true, "depth" : 12.95 * mm});
        }
        {
            var Q0;
            Q0=makeQuery(id+"F1.opExtrude","SWEPT_FACE",FACE,{"disambiguationData":[OSD([sQuery(id+"F0.wireOp",EDGE,"E2"),sQuery(id+"F0.wireOp",EDGE,"E3")])]});
            var sketch = newSketch(context, id + "F18", { "sketchPlane" : qUnion([Q0])});
            skLineSegment(sketch, "E284", {"start": v(-11.11, -36.78) * mm, "end": v(-14.29, -36.78) * mm});
            skLineSegment(sketch, "E285", {"start": v(-14.29, -36.78) * mm, "end": v(-14.29, -44.4) * mm});
            skLineSegment(sketch, "E286", {"start": v(-14.29, -44.4) * mm, "end": v(-11.11, -44.4) * mm});
            skLineSegment(sketch, "E287", {"start": v(-11.11, -44.4) * mm, "end": v(-11.11, -36.78) * mm});
            skLineSegment(sketch, "E288", {"start": v(-19.43, -44.9) * mm, "end": v(-22.6, -44.9) * mm});
            skLineSegment(sketch, "E289", {"start": v(-22.6, -44.9) * mm, "end": v(-22.6, -52.52) * mm});
            skLineSegment(sketch, "E290", {"start": v(-22.6, -52.52) * mm, "end": v(-19.43, -52.52) * mm});
            skLineSegment(sketch, "E291", {"start": v(-19.43, -52.52) * mm, "end": v(-19.43, -44.9) * mm});
            skLineSegment(sketch, "E292", {"start": v(-16.51, -47.44) * mm, "end": v(-16.51, -50.62) * mm});
            skLineSegment(sketch, "E293", {"start": v(-16.51, -50.62) * mm, "end": v(-8.89, -50.62) * mm});
            skLineSegment(sketch, "E294", {"start": v(-8.89, -50.62) * mm, "end": v(-8.9, -47.44) * mm});
            skLineSegment(sketch, "E295", {"start": v(-8.9, -47.44) * mm, "end": v(-16.51, -47.44) * mm});
            skLineSegment(sketch, "E296", {"start": v(-5.97, -44.9) * mm, "end": v(-5.97, -52.52) * mm});
            skLineSegment(sketch, "E297", {"start": v(-5.97, -52.52) * mm, "end": v(-2.8, -52.52) * mm});
            skLineSegment(sketch, "E298", {"start": v(-2.8, -52.52) * mm, "end": v(-2.8, -44.9) * mm});
            skLineSegment(sketch, "E299", {"start": v(-2.8, -44.9) * mm, "end": v(-5.97, -44.9) * mm});
            skLineSegment(sketch, "E300", {"start": v(-16.51, -55.45) * mm, "end": v(-16.51, -58.62) * mm});
            skLineSegment(sketch, "E301", {"start": v(-16.51, -58.62) * mm, "end": v(-8.89, -58.62) * mm});
            skLineSegment(sketch, "E302", {"start": v(-8.89, -58.62) * mm, "end": v(-8.9, -55.45) * mm});
            skLineSegment(sketch, "E303", {"start": v(-8.9, -55.45) * mm, "end": v(-16.51, -55.45) * mm});
            skLineSegment(sketch, "E304", {"start": v(-10.1, -35.76) * mm, "end": v(-15.3, -35.76) * mm});
            skLineSegment(sketch, "E305", {"start": v(-15.3, -35.76) * mm, "end": v(-15.3, -45.41) * mm});
            skLineSegment(sketch, "E306", {"start": v(-15.3, -45.41) * mm, "end": v(-10.1, -45.41) * mm});
            skLineSegment(sketch, "E307", {"start": v(-10.1, -45.41) * mm, "end": v(-10.1, -35.76) * mm});
            skLineSegment(sketch, "E308", {"start": v(-6.99, -43.89) * mm, "end": v(-6.98, -53.54) * mm});
            skLineSegment(sketch, "E309", {"start": v(-6.98, -53.54) * mm, "end": v(-1.78, -53.54) * mm});
            skLineSegment(sketch, "E310", {"start": v(-1.78, -53.54) * mm, "end": v(-1.78, -43.89) * mm});
            skLineSegment(sketch, "E311", {"start": v(-1.78, -43.89) * mm, "end": v(-6.99, -43.89) * mm});
            skLineSegment(sketch, "E312", {"start": v(-17.53, -46.43) * mm, "end": v(-17.53, -51.64) * mm});
            skLineSegment(sketch, "E313", {"start": v(-17.53, -51.64) * mm, "end": v(-7.87, -51.64) * mm});
            skLineSegment(sketch, "E314", {"start": v(-7.87, -51.64) * mm, "end": v(-7.87, -46.43) * mm});
            skLineSegment(sketch, "E315", {"start": v(-7.87, -46.43) * mm, "end": v(-17.53, -46.43) * mm});
            skLineSegment(sketch, "E316", {"start": v(-23.62, -43.89) * mm, "end": v(-18.42, -43.89) * mm});
            skLineSegment(sketch, "E317", {"start": v(-18.42, -43.89) * mm, "end": v(-18.41, -53.54) * mm});
            skLineSegment(sketch, "E318", {"start": v(-18.41, -53.54) * mm, "end": v(-23.62, -53.54) * mm});
            skLineSegment(sketch, "E319", {"start": v(-23.62, -53.54) * mm, "end": v(-23.62, -43.89) * mm});
            skLineSegment(sketch, "E320", {"start": v(-17.53, -54.43) * mm, "end": v(-17.53, -59.64) * mm});
            skLineSegment(sketch, "E321", {"start": v(-17.53, -59.64) * mm, "end": v(-7.87, -59.64) * mm});
            skLineSegment(sketch, "E322", {"start": v(-7.87, -59.64) * mm, "end": v(-7.87, -54.43) * mm});
            skLineSegment(sketch, "E323", {"start": v(-7.87, -54.43) * mm, "end": v(-17.53, -54.43) * mm});
            skSolve(sketch);
        }
        {
            var Q0;
            Q0 = qSketchRegion(id + "F18", true);
            extrude(context, id + "F19", {"entities" : qUnion([Q0]), "operationType" : NewBodyOperationType.ADD, "oppositeDirection" : true, "depth" : 12.95 * mm});
        }
        {
            var Q0;
            Q0=makeQuery(id+"F1.opExtrude","CAP_FACE",FACE,{"disambiguationData":[OSD([sQuery(id+"F0.wireOp",EDGE,"E0"),sQuery(id+"F0.wireOp",EDGE,"E1"),sQuery(id+"F0.wireOp",EDGE,"E2"),sQuery(id+"F0.wireOp",EDGE,"E3"),sQuery(id+"F0.wireOp",EDGE,"E4"),sQuery(id+"F0.wireOp",EDGE,"E5")])],"isStart":true});
            var sketch = newSketch(context, id + "F20", { "sketchPlane" : qUnion([Q0])});
            skArc(sketch, "E324", {"start": v(-29.36, 71.73) * mm, "mid": v(-30.84, 68.14) * mm, "end": v(-34.44, 66.65) * mm});
            skLineSegment(sketch, "E325", {"start": v(-34.44, 71.73) * mm, "end": v(-34.44, 66.65) * mm});
            skLineSegment(sketch, "E326", {"start": v(-29.36, 71.73) * mm, "end": v(-34.44, 71.73) * mm});
            skArc(sketch, "E327", {"start": v(37.7, 71.73) * mm, "mid": v(39.19, 68.14) * mm, "end": v(42.78, 66.65) * mm});
            skLineSegment(sketch, "E328", {"start": v(42.78, 71.73) * mm, "end": v(37.7, 71.73) * mm});
            skLineSegment(sketch, "E329", {"start": v(42.78, 66.65) * mm, "end": v(42.78, 71.73) * mm});
            skArc(sketch, "E330", {"start": v(-29.36, -71.53) * mm, "mid": v(-30.84, -67.94) * mm, "end": v(-34.44, -66.45) * mm});
            skLineSegment(sketch, "E331", {"start": v(-34.44, -66.45) * mm, "end": v(-34.44, -71.53) * mm});
            skLineSegment(sketch, "E332", {"start": v(-29.36, -71.53) * mm, "end": v(-34.44, -71.53) * mm});
            skArc(sketch, "E333", {"start": v(37.7, -71.53) * mm, "mid": v(39.19, -67.94) * mm, "end": v(42.78, -66.45) * mm});
            skLineSegment(sketch, "E334", {"start": v(42.78, -66.45) * mm, "end": v(42.78, -71.53) * mm});
            skLineSegment(sketch, "E335", {"start": v(37.7, -71.53) * mm, "end": v(42.78, -71.53) * mm});
            skSolve(sketch);
        }
        {
            var Q0;
            Q0 = qSketchRegion(id + "F20", true);
            extrude(context, id + "F21", {"entities" : qUnion([Q0]), "operationType" : NewBodyOperationType.ADD, "oppositeDirection" : true, "depth" : 25.4 * mm});
        }
        {
            var Q0;
            Q0=makeQuery(id+"F1.opExtrude","SWEPT_FACE",FACE,{"disambiguationData":[OSD([sQuery(id+"F0.wireOp",EDGE,"E0")])]});
            var sketch = newSketch(context, id + "F22", { "sketchPlane" : qUnion([Q0])});
            skLineSegment(sketch, "E336", {"start": v(-20.05, 0) * mm, "end": v(-20.05, -23.5) * mm});
            skLineSegment(sketch, "E337", {"start": v(-20.05, -23.5) * mm, "end": v(11.7, -23.5) * mm});
            skLineSegment(sketch, "E338", {"start": v(11.7, -23.5) * mm, "end": v(11.7, 0) * mm});
            skLineSegment(sketch, "E339", {"start": v(11.7, 0) * mm, "end": v(-20.05, 0) * mm});
            skSolve(sketch);
        }
        {
            var Q0;
            Q0 = qSketchRegion(id + "F22", true);
            extrude(context, id + "F23", {"entities" : qUnion([Q0]), "operationType" : NewBodyOperationType.ADD, "depth" : 3.3 * mm});
        }
        {
            var Q0;
            Q0=makeQuery(id+"F23.opExtrude","CAP_FACE",FACE,{"disambiguationData":[OSD([sQuery(id+"F22.wireOp",EDGE,"E336"),sQuery(id+"F22.wireOp",EDGE,"E337"),sQuery(id+"F22.wireOp",EDGE,"E338"),sQuery(id+"F22.wireOp",EDGE,"E339")])],"isStart":false});
            var sketch = newSketch(context, id + "F24", { "sketchPlane" : qUnion([Q0])});
            skLineSegment(sketch, "E340", {"start": v(-18.78, 0) * mm, "end": v(-18.78, -22.23) * mm});
            skLineSegment(sketch, "E341", {"start": v(-18.78, -22.23) * mm, "end": v(10.43, -22.23) * mm});
            skLineSegment(sketch, "E342", {"start": v(10.43, -22.23) * mm, "end": v(10.43, 0) * mm});
            skLineSegment(sketch, "E343", {"start": v(-18.78, 0) * mm, "end": v(10.43, 0) * mm});
            skSolve(sketch);
        }
        {
            var Q0;
            Q0 = qSketchRegion(id + "F24", true);
            extrude(context, id + "F25", {"entities" : qUnion([Q0]), "operationType" : NewBodyOperationType.REMOVE, "oppositeDirection" : true, "depth" : 2.16 * mm});
        }
        {
            var Q0;
            Q0=makeQuery(id+"F25.boolean.opBoolean","COPY",FACE,{"derivedFrom":makeQuery(id+"F25.opExtrude","CAP_FACE",FACE,{"disambiguationData":[OSD([sQuery(id+"F24.wireOp",EDGE,"E340"),sQuery(id+"F24.wireOp",EDGE,"E341"),sQuery(id+"F24.wireOp",EDGE,"E342"),sQuery(id+"F24.wireOp",EDGE,"E343")])],"isStart":false})});
            var sketch = newSketch(context, id + "F26", { "sketchPlane" : qUnion([Q0])});
            skArc(sketch, "E344", {"start": v(-11.82, 0) * mm, "mid": v(-4.17, -18.41) * mm, "end": v(3.47, 0) * mm});
            skLineSegment(sketch, "E345", {"start": v(-11.82, 0) * mm, "end": v(3.47, 0) * mm});
            skSolve(sketch);
        }
        {
            var Q0;
            Q0 = qSketchRegion(id + "F26", true);
            extrude(context, id + "F27", {"entities" : qUnion([Q0]), "operationType" : NewBodyOperationType.REMOVE, "oppositeDirection" : true, "depth" : 25.4 * mm});
        }
        {
            var Q0;
            Q0=makeQuery(id+"F9.boolean.opBoolean","MERGE",FACE,{"derivedFrom":[makeQuery(id+"F1.opExtrude","SWEPT_FACE",FACE,{"disambiguationData":[OSD([sQuery(id+"F0.wireOp",EDGE,"E1"),sQuery(id+"F0.wireOp",EDGE,"E5")])]}),makeQuery(id+"F9.opExtrude","CAP_FACE",FACE,{"disambiguationData":[OSD([sQuery(id+"F8.wireOp",EDGE,"E64"),sQuery(id+"F8.wireOp",EDGE,"E65"),sQuery(id+"F8.wireOp",EDGE,"E66"),sQuery(id+"F8.wireOp",EDGE,"E67")])],"isStart":true}),makeQuery(id+"F9.opExtrude","CAP_FACE",FACE,{"disambiguationData":[OSD([sQuery(id+"F8.wireOp",EDGE,"E68"),sQuery(id+"F8.wireOp",EDGE,"E69"),sQuery(id+"F8.wireOp",EDGE,"E70"),sQuery(id+"F8.wireOp",EDGE,"E71")])],"isStart":true}),makeQuery(id+"F9.opExtrude","CAP_FACE",FACE,{"disambiguationData":[OSD([sQuery(id+"F8.wireOp",EDGE,"E72"),sQuery(id+"F8.wireOp",EDGE,"E73"),sQuery(id+"F8.wireOp",EDGE,"E74"),sQuery(id+"F8.wireOp",EDGE,"E75")])],"isStart":true}),makeQuery(id+"F9.opExtrude","CAP_FACE",FACE,{"disambiguationData":[OSD([sQuery(id+"F8.wireOp",EDGE,"E76"),sQuery(id+"F8.wireOp",EDGE,"E77"),sQuery(id+"F8.wireOp",EDGE,"E78"),sQuery(id+"F8.wireOp",EDGE,"E79")])],"isStart":true})]});
            var sketch = newSketch(context, id + "F28", { "sketchPlane" : qUnion([Q0])});
            skSolve(sketch);
        }
        {
            var Q0;
            Q0=makeQuery(id+"F1.opExtrude","SWEPT_FACE",FACE,{"disambiguationData":[OSD([sQuery(id+"F0.wireOp",EDGE,"E2"),sQuery(id+"F0.wireOp",EDGE,"E3")])]});
            var sketch = newSketch(context, id + "F29", { "sketchPlane" : qUnion([Q0])});
            skLineSegment(sketch, "E346", {"start": v(0, 24.46) * mm, "end": v(0, 57.48) * mm});
            skLineSegment(sketch, "E347", {"start": v(-22.86, 57.48) * mm, "end": v(-22.86, 24.46) * mm});
            skLineSegment(sketch, "E348", {"start": v(0, 57.48) * mm, "end": v(-22.86, 57.48) * mm});
            skLineSegment(sketch, "E349", {"start": v(0, 24.46) * mm, "end": v(-22.86, 24.46) * mm});
            skSolve(sketch);
        }
        {
            var Q0;
            Q0 = qSketchRegion(id + "F29", true);
            extrude(context, id + "F30", {"entities" : qUnion([Q0]), "operationType" : NewBodyOperationType.REMOVE, "oppositeDirection" : true, "depth" : 25.4 * mm});
        }
        {
            var Q0;
            Q0=makeQuery(id+"F1.opExtrude","SWEPT_FACE",FACE,{"disambiguationData":[OSD([sQuery(id+"F0.wireOp",EDGE,"E2"),sQuery(id+"F0.wireOp",EDGE,"E3")])]});
            var sketch = newSketch(context, id + "F31", { "sketchPlane" : qUnion([Q0])});
            skLineSegment(sketch, "E350", {"start": v(-22.86, 57.48) * mm, "end": v(-22.86, 57.99) * mm});
            skLineSegment(sketch, "E351", {"start": v(-22.86, 57.99) * mm, "end": v(0, 57.99) * mm});
            skLineSegment(sketch, "E352", {"start": v(0, 57.99) * mm, "end": v(0, 57.48) * mm});
            skLineSegment(sketch, "E353", {"start": v(0, 57.48) * mm, "end": v(-22.86, 57.48) * mm});
            skLineSegment(sketch, "E354", {"start": v(-22.86, 24.46) * mm, "end": v(-22.86, 23.95) * mm});
            skLineSegment(sketch, "E355", {"start": v(-22.86, 23.95) * mm, "end": v(0, 23.95) * mm});
            skLineSegment(sketch, "E356", {"start": v(0, 23.95) * mm, "end": v(0, 24.46) * mm});
            skLineSegment(sketch, "E357", {"start": v(0, 24.46) * mm, "end": v(-22.86, 24.46) * mm});
            skSolve(sketch);
        }
        {
            var Q0;
            Q0 = qSketchRegion(id + "F31", true);
            extrude(context, id + "F32", {"entities" : qUnion([Q0]), "operationType" : NewBodyOperationType.REMOVE, "oppositeDirection" : true, "depth" : 1.02 * mm});
        }
        {
            var Q0;
            {var subQ1=sQuery(id+"F0.wireOp",EDGE,"E1");Q0=makeQuery(id+"F28.imprint","IMPRINT",FACE,{"disambiguationData":[TD([[makeQuery(id+"F28.imprint","IMPRINT",EDGE,{"derivedFrom":makeQuery(id+"F1.opExtrude","SWEPT_EDGE",EDGE,{"disambiguationData":[OSD([sQuery(id+"F0.wireOp",EDGE,"E0"),subQ1])]})}),1.0]])]});}
            var sketch = newSketch(context, id + "F33", { "sketchPlane" : qUnion([Q0])});
            skLineSegment(sketch, "E358", {"start": v(0, 41.9) * mm, "end": v(22.86, 41.9) * mm});
            skLineSegment(sketch, "E359", {"start": v(22.86, 41.9) * mm, "end": v(22.86, 24.37) * mm});
            skLineSegment(sketch, "E360", {"start": v(22.86, 24.37) * mm, "end": v(0, 24.37) * mm});
            skLineSegment(sketch, "E361", {"start": v(0, 24.37) * mm, "end": v(0, 41.9) * mm});
            skSolve(sketch);
        }
        {
            var Q0;
            Q0=makeQuery(id+"F32.boolean.opBoolean","COPY",FACE,{"derivedFrom":makeQuery(id+"F32.opExtrude","CAP_FACE",FACE,{"disambiguationData":[OSD([sQuery(id+"F31.wireOp",EDGE,"E350"),sQuery(id+"F31.wireOp",EDGE,"E351"),sQuery(id+"F31.wireOp",EDGE,"E352"),sQuery(id+"F31.wireOp",EDGE,"E353")])],"isStart":false})});
            var sketch = newSketch(context, id + "F34", { "sketchPlane" : qUnion([Q0])});
            skLineSegment(sketch, "E362", {"start": v(-22.86, 57.48) * mm, "end": v(-22.86, 56.97) * mm});
            skLineSegment(sketch, "E363", {"start": v(-22.86, 57.48) * mm, "end": v(0, 57.48) * mm});
            skLineSegment(sketch, "E364", {"start": v(0, 57.48) * mm, "end": v(0, 56.97) * mm});
            skLineSegment(sketch, "E365", {"start": v(0, 56.97) * mm, "end": v(-22.86, 56.97) * mm});
            skSolve(sketch);
        }
        {
            var Q0;
            Q0 = qSketchRegion(id + "F34", true);
            extrude(context, id + "F35", {"entities" : qUnion([Q0]), "operationType" : NewBodyOperationType.ADD, "oppositeDirection" : true, "depth" : 1.02 * mm});
        }
        {
            var Q0;
            Q0=makeQuery(id+"F32.boolean.opBoolean","COPY",FACE,{"derivedFrom":makeQuery(id+"F32.opExtrude","CAP_FACE",FACE,{"disambiguationData":[OSD([sQuery(id+"F31.wireOp",EDGE,"E354"),sQuery(id+"F31.wireOp",EDGE,"E355"),sQuery(id+"F31.wireOp",EDGE,"E356"),sQuery(id+"F31.wireOp",EDGE,"E357")])],"isStart":false})});
            var sketch = newSketch(context, id + "F36", { "sketchPlane" : qUnion([Q0])});
            skLineSegment(sketch, "E366", {"start": v(-22.86, 24.46) * mm, "end": v(0, 24.46) * mm});
            skLineSegment(sketch, "E367", {"start": v(0, 24.46) * mm, "end": v(0, 25.22) * mm});
            skLineSegment(sketch, "E368", {"start": v(-22.86, 24.46) * mm, "end": v(-22.86, 25.22) * mm});
            skLineSegment(sketch, "E369", {"start": v(-22.86, 25.22) * mm, "end": v(0, 25.22) * mm});
            skSolve(sketch);
        }
        {
            var Q0;
            Q0 = qSketchRegion(id + "F36", true);
            extrude(context, id + "F37", {"entities" : qUnion([Q0]), "operationType" : NewBodyOperationType.ADD, "oppositeDirection" : true, "depth" : 1.02 * mm});
        }
        {
            var Q0;
            Q0 = qSketchRegion(id + "F33", true);
            extrude(context, id + "F38", {"entities" : qUnion([Q0]), "operationType" : NewBodyOperationType.REMOVE, "oppositeDirection" : true, "depth" : 25.4 * mm});
        }
        {
            var Q0;
            {var subQ21=sQuery(id+"F20.wireOp",EDGE,"E327");var subQ23=sQuery(id+"F0.wireOp",EDGE,"E5");var subQ24=sQuery(id+"F0.wireOp",EDGE,"E1");var subQ34=sQuery(id+"F0.wireOp",EDGE,"E0");var subQ35=makeQuery(id+"F1.opExtrude","SWEPT_FACE",FACE,{"disambiguationData":[OSD([subQ34])]});var subQ38=sQuery(id+"F22.wireOp",EDGE,"E339");var subQ41=sQuery(id+"F0.wireOp",EDGE,"E3");var subQ42=sQuery(id+"F0.wireOp",EDGE,"E2");var subQ43=sQuery(id+"F0.wireOp",EDGE,"E4");var subQ44=sQuery(id+"F20.wireOp",EDGE,"E330");var subQ45=sQuery(id+"F20.wireOp",EDGE,"E333");Q0=makeQuery(id+"F38.boolean.opBoolean","SPLIT",FACE,{"disambiguationData":[TD([subQ35])],"derivedFrom":makeQuery(id+"F37.boolean.opBoolean","MERGE",FACE,{"derivedFrom":[makeQuery(id+"F30.boolean.opBoolean","SPLIT",FACE,{"disambiguationData":[TD([makeQuery(id+"F1.opExtrude","SWEPT_FACE",FACE,{"disambiguationData":[OSD([subQ43])]})])],"derivedFrom":makeQuery(id+"F23.boolean.opBoolean","MERGE",FACE,{"derivedFrom":[makeQuery(id+"F21.boolean.opBoolean","MERGE",FACE,{"derivedFrom":[makeQuery(id+"F1.opExtrude","CAP_FACE",FACE,{"disambiguationData":[OSD([subQ34,subQ24,subQ42,subQ41,subQ43,subQ23])],"isStart":true}),makeQuery(id+"F21.opExtrude","CAP_FACE",FACE,{"disambiguationData":[OSD([sQuery(id+"F20.wireOp",EDGE,"E324"),sQuery(id+"F20.wireOp",EDGE,"E325"),sQuery(id+"F20.wireOp",EDGE,"E326")])],"isStart":true}),makeQuery(id+"F21.opExtrude","CAP_FACE",FACE,{"disambiguationData":[OSD([subQ21,sQuery(id+"F20.wireOp",EDGE,"E328"),sQuery(id+"F20.wireOp",EDGE,"E329")])],"isStart":true}),makeQuery(id+"F21.opExtrude","CAP_FACE",FACE,{"disambiguationData":[OSD([subQ44,sQuery(id+"F20.wireOp",EDGE,"E331"),sQuery(id+"F20.wireOp",EDGE,"E332")])],"isStart":true}),makeQuery(id+"F21.opExtrude","CAP_FACE",FACE,{"disambiguationData":[OSD([subQ45,sQuery(id+"F20.wireOp",EDGE,"E334"),sQuery(id+"F20.wireOp",EDGE,"E335")])],"isStart":true})]}),makeQuery(id+"F23.opExtrude","SWEPT_FACE",FACE,{"disambiguationData":[OSD([subQ38])]})]})}),makeQuery(id+"F37.opExtrude","SWEPT_FACE",FACE,{"disambiguationData":[OSD([sQuery(id+"F36.wireOp",EDGE,"E367")])]})]})});}
            var sketch = newSketch(context, id + "F39", { "sketchPlane" : qUnion([Q0])});
            skLineSegment(sketch, "E370", {"start": v(42.78, 41.9) * mm, "end": v(43.8, 41.9) * mm});
            skLineSegment(sketch, "E371", {"start": v(43.8, 41.9) * mm, "end": v(43.8, 40.88) * mm});
            skLineSegment(sketch, "E372", {"start": v(43.8, 40.88) * mm, "end": v(42.78, 40.88) * mm});
            skLineSegment(sketch, "E373", {"start": v(42.78, 40.88) * mm, "end": v(42.78, 41.9) * mm});
            skSolve(sketch);
        }
        {
            var Q0;
            Q0 = qSketchRegion(id + "F39", true);
            extrude(context, id + "F40", {"entities" : qUnion([Q0]), "operationType" : NewBodyOperationType.ADD, "oppositeDirection" : true, "depth" : 25.4 * mm});
        }
        {
            var Q0;
            {var subQ2=sQuery(id+"F36.wireOp",EDGE,"E367");var subQ20=sQuery(id+"F20.wireOp",EDGE,"E330");var subQ25=sQuery(id+"F0.wireOp",EDGE,"E4");var subQ26=makeQuery(id+"F1.opExtrude","SWEPT_FACE",FACE,{"disambiguationData":[OSD([subQ25])]});var subQ33=sQuery(id+"F0.wireOp",EDGE,"E3");var subQ34=sQuery(id+"F0.wireOp",EDGE,"E2");var subQ36=sQuery(id+"F0.wireOp",EDGE,"E5");var subQ37=sQuery(id+"F0.wireOp",EDGE,"E1");var subQ42=sQuery(id+"F20.wireOp",EDGE,"E333");var subQ44=sQuery(id+"F22.wireOp",EDGE,"E339");var subQ46=sQuery(id+"F20.wireOp",EDGE,"E327");var subQ48=sQuery(id+"F0.wireOp",EDGE,"E0");Q0=makeQuery(id+"F38.boolean.opBoolean","SPLIT",FACE,{"disambiguationData":[TD([subQ26])],"derivedFrom":makeQuery(id+"F37.boolean.opBoolean","MERGE",FACE,{"derivedFrom":[makeQuery(id+"F30.boolean.opBoolean","SPLIT",FACE,{"disambiguationData":[TD([subQ26])],"derivedFrom":makeQuery(id+"F23.boolean.opBoolean","MERGE",FACE,{"derivedFrom":[makeQuery(id+"F21.boolean.opBoolean","MERGE",FACE,{"derivedFrom":[makeQuery(id+"F1.opExtrude","CAP_FACE",FACE,{"disambiguationData":[OSD([subQ48,subQ37,subQ34,subQ33,subQ25,subQ36])],"isStart":true}),makeQuery(id+"F21.opExtrude","CAP_FACE",FACE,{"disambiguationData":[OSD([sQuery(id+"F20.wireOp",EDGE,"E324"),sQuery(id+"F20.wireOp",EDGE,"E325"),sQuery(id+"F20.wireOp",EDGE,"E326")])],"isStart":true}),makeQuery(id+"F21.opExtrude","CAP_FACE",FACE,{"disambiguationData":[OSD([subQ46,sQuery(id+"F20.wireOp",EDGE,"E328"),sQuery(id+"F20.wireOp",EDGE,"E329")])],"isStart":true}),makeQuery(id+"F21.opExtrude","CAP_FACE",FACE,{"disambiguationData":[OSD([subQ20,sQuery(id+"F20.wireOp",EDGE,"E331"),sQuery(id+"F20.wireOp",EDGE,"E332")])],"isStart":true}),makeQuery(id+"F21.opExtrude","CAP_FACE",FACE,{"disambiguationData":[OSD([subQ42,sQuery(id+"F20.wireOp",EDGE,"E334"),sQuery(id+"F20.wireOp",EDGE,"E335")])],"isStart":true})]}),makeQuery(id+"F23.opExtrude","SWEPT_FACE",FACE,{"disambiguationData":[OSD([subQ44])]})]})}),makeQuery(id+"F37.opExtrude","SWEPT_FACE",FACE,{"disambiguationData":[OSD([subQ2])]})]})});}
            var sketch = newSketch(context, id + "F41", { "sketchPlane" : qUnion([Q0])});
            skLineSegment(sketch, "E374", {"start": v(42.78, 24.37) * mm, "end": v(42.78, 25.64) * mm});
            skLineSegment(sketch, "E375", {"start": v(42.78, 25.64) * mm, "end": v(43.8, 25.64) * mm});
            skLineSegment(sketch, "E376", {"start": v(43.8, 25.64) * mm, "end": v(43.8, 24.37) * mm});
            skLineSegment(sketch, "E377", {"start": v(43.8, 24.37) * mm, "end": v(42.78, 24.37) * mm});
            skSolve(sketch);
        }
        {
            var Q0;
            Q0 = qSketchRegion(id + "F41", true);
            extrude(context, id + "F42", {"entities" : qUnion([Q0]), "operationType" : NewBodyOperationType.ADD, "oppositeDirection" : true, "depth" : 25.4 * mm});
        }
        {
            var Q0;
            Q0=makeQuery(id+"F1.opExtrude","SWEPT_FACE",FACE,{"disambiguationData":[OSD([sQuery(id+"F0.wireOp",EDGE,"E2"),sQuery(id+"F0.wireOp",EDGE,"E3")])]});
            var sketch = newSketch(context, id + "F43", { "sketchPlane" : qUnion([Q0])});
            skLineSegment(sketch, "E378", {"start": v(0, 0.43) * mm, "end": v(-23.88, 0.43) * mm});
            skLineSegment(sketch, "E379", {"start": v(-23.88, 0.43) * mm, "end": v(-23.88, -61.29) * mm});
            skLineSegment(sketch, "E380", {"start": v(-23.88, -61.29) * mm, "end": v(0, -61.29) * mm});
            skLineSegment(sketch, "E381", {"start": v(0, -61.29) * mm, "end": v(0, 0.43) * mm});
            skSolve(sketch);
        }
        {
            var Q0;
            Q0 = qSketchRegion(id + "F43", true);
            extrude(context, id + "F44", {"entities" : qUnion([Q0]), "operationType" : NewBodyOperationType.REMOVE, "endBound" : BoundingType.THROUGH_ALL, "oppositeDirection" : true, "depth" : 25.4 * mm});
        }
        {
            var Q0;
            {var subQ10=sQuery(id+"F20.wireOp",EDGE,"E333");var subQ21=sQuery(id+"F0.wireOp",EDGE,"E5");var subQ22=sQuery(id+"F0.wireOp",EDGE,"E1");var subQ30=sQuery(id+"F0.wireOp",EDGE,"E3");var subQ31=sQuery(id+"F0.wireOp",EDGE,"E2");var subQ33=sQuery(id+"F0.wireOp",EDGE,"E4");var subQ34=makeQuery(id+"F1.opExtrude","SWEPT_FACE",FACE,{"disambiguationData":[OSD([subQ33])]});var subQ37=sQuery(id+"F20.wireOp",EDGE,"E330");var subQ42=sQuery(id+"F36.wireOp",EDGE,"E367");var subQ45=sQuery(id+"F41.wireOp",EDGE,"E374");var subQ47=sQuery(id+"F22.wireOp",EDGE,"E339");var subQ49=sQuery(id+"F20.wireOp",EDGE,"E327");var subQ51=sQuery(id+"F0.wireOp",EDGE,"E0");Q0=makeQuery(id+"F44.boolean.opBoolean","SPLIT",FACE,{"disambiguationData":[TD([subQ34])],"derivedFrom":makeQuery(id+"F42.boolean.opBoolean","MERGE",FACE,{"derivedFrom":[makeQuery(id+"F38.boolean.opBoolean","SPLIT",FACE,{"disambiguationData":[TD([subQ34])],"derivedFrom":makeQuery(id+"F37.boolean.opBoolean","MERGE",FACE,{"derivedFrom":[makeQuery(id+"F30.boolean.opBoolean","SPLIT",FACE,{"disambiguationData":[TD([subQ34])],"derivedFrom":makeQuery(id+"F23.boolean.opBoolean","MERGE",FACE,{"derivedFrom":[makeQuery(id+"F21.boolean.opBoolean","MERGE",FACE,{"derivedFrom":[makeQuery(id+"F1.opExtrude","CAP_FACE",FACE,{"disambiguationData":[OSD([subQ51,subQ22,subQ31,subQ30,subQ33,subQ21])],"isStart":true}),makeQuery(id+"F21.opExtrude","CAP_FACE",FACE,{"disambiguationData":[OSD([sQuery(id+"F20.wireOp",EDGE,"E324"),sQuery(id+"F20.wireOp",EDGE,"E325"),sQuery(id+"F20.wireOp",EDGE,"E326")])],"isStart":true}),makeQuery(id+"F21.opExtrude","CAP_FACE",FACE,{"disambiguationData":[OSD([subQ49,sQuery(id+"F20.wireOp",EDGE,"E328"),sQuery(id+"F20.wireOp",EDGE,"E329")])],"isStart":true}),makeQuery(id+"F21.opExtrude","CAP_FACE",FACE,{"disambiguationData":[OSD([subQ37,sQuery(id+"F20.wireOp",EDGE,"E331"),sQuery(id+"F20.wireOp",EDGE,"E332")])],"isStart":true}),makeQuery(id+"F21.opExtrude","CAP_FACE",FACE,{"disambiguationData":[OSD([subQ10,sQuery(id+"F20.wireOp",EDGE,"E334"),sQuery(id+"F20.wireOp",EDGE,"E335")])],"isStart":true})]}),makeQuery(id+"F23.opExtrude","SWEPT_FACE",FACE,{"disambiguationData":[OSD([subQ47])]})]})}),makeQuery(id+"F37.opExtrude","SWEPT_FACE",FACE,{"disambiguationData":[OSD([subQ42])]})]})}),makeQuery(id+"F42.opExtrude","CAP_FACE",FACE,{"disambiguationData":[OSD([subQ45,sQuery(id+"F41.wireOp",EDGE,"E375"),sQuery(id+"F41.wireOp",EDGE,"E376"),sQuery(id+"F41.wireOp",EDGE,"E377")])],"isStart":true})]})});}
            var sketch = newSketch(context, id + "F45", { "sketchPlane" : qUnion([Q0])});
            skLineSegment(sketch, "E382", {"start": v(-34.44, -61.29) * mm, "end": v(-34.44, -60.02) * mm});
            skLineSegment(sketch, "E383", {"start": v(-34.44, -60.02) * mm, "end": v(-35.45, -60.02) * mm});
            skLineSegment(sketch, "E384", {"start": v(-35.45, -60.02) * mm, "end": v(-35.45, -61.29) * mm});
            skLineSegment(sketch, "E385", {"start": v(-35.45, -61.29) * mm, "end": v(-34.44, -61.29) * mm});
            skLineSegment(sketch, "E386", {"start": v(42.78, -61.29) * mm, "end": v(42.78, -60.02) * mm});
            skLineSegment(sketch, "E387", {"start": v(42.78, -60.02) * mm, "end": v(43.8, -60.02) * mm});
            skLineSegment(sketch, "E388", {"start": v(43.8, -60.02) * mm, "end": v(43.8, -61.29) * mm});
            skLineSegment(sketch, "E389", {"start": v(43.8, -61.29) * mm, "end": v(42.78, -61.29) * mm});
            skSolve(sketch);
        }
        {
            var Q0;
            Q0 = qSketchRegion(id + "F45", true);
            extrude(context, id + "F46", {"entities" : qUnion([Q0]), "operationType" : NewBodyOperationType.ADD, "oppositeDirection" : true, "depth" : 25.4 * mm});
        }
        {
            var Q0;
            {var subQ0=sQuery(id+"F31.wireOp",EDGE,"E355");var subQ1=makeQuery(id+"F32.boolean.opBoolean","COPY",FACE,{"derivedFrom":makeQuery(id+"F32.opExtrude","SWEPT_FACE",FACE,{"disambiguationData":[OSD([subQ0])]})});var subQ7=sQuery(id+"F0.wireOp",EDGE,"E3");var subQ8=sQuery(id+"F0.wireOp",EDGE,"E2");var subQ11=sQuery(id+"F36.wireOp",EDGE,"E367");var subQ30=sQuery(id+"F20.wireOp",EDGE,"E330");var subQ34=sQuery(id+"F0.wireOp",EDGE,"E4");var subQ35=makeQuery(id+"F1.opExtrude","SWEPT_FACE",FACE,{"disambiguationData":[OSD([subQ34])]});var subQ42=sQuery(id+"F0.wireOp",EDGE,"E5");var subQ43=sQuery(id+"F0.wireOp",EDGE,"E1");var subQ48=sQuery(id+"F20.wireOp",EDGE,"E333");var subQ50=sQuery(id+"F22.wireOp",EDGE,"E339");var subQ52=sQuery(id+"F20.wireOp",EDGE,"E327");var subQ54=sQuery(id+"F0.wireOp",EDGE,"E0");Q0=makeQuery(id+"F44.boolean.opBoolean","SPLIT",FACE,{"disambiguationData":[TD([subQ1])],"derivedFrom":makeQuery(id+"F42.boolean.opBoolean","MERGE",FACE,{"derivedFrom":[makeQuery(id+"F38.boolean.opBoolean","SPLIT",FACE,{"disambiguationData":[TD([subQ35])],"derivedFrom":makeQuery(id+"F37.boolean.opBoolean","MERGE",FACE,{"derivedFrom":[makeQuery(id+"F30.boolean.opBoolean","SPLIT",FACE,{"disambiguationData":[TD([subQ35])],"derivedFrom":makeQuery(id+"F23.boolean.opBoolean","MERGE",FACE,{"derivedFrom":[makeQuery(id+"F21.boolean.opBoolean","MERGE",FACE,{"derivedFrom":[makeQuery(id+"F1.opExtrude","CAP_FACE",FACE,{"disambiguationData":[OSD([subQ54,subQ43,subQ8,subQ7,subQ34,subQ42])],"isStart":true}),makeQuery(id+"F21.opExtrude","CAP_FACE",FACE,{"disambiguationData":[OSD([sQuery(id+"F20.wireOp",EDGE,"E324"),sQuery(id+"F20.wireOp",EDGE,"E325"),sQuery(id+"F20.wireOp",EDGE,"E326")])],"isStart":true}),makeQuery(id+"F21.opExtrude","CAP_FACE",FACE,{"disambiguationData":[OSD([subQ52,sQuery(id+"F20.wireOp",EDGE,"E328"),sQuery(id+"F20.wireOp",EDGE,"E329")])],"isStart":true}),makeQuery(id+"F21.opExtrude","CAP_FACE",FACE,{"disambiguationData":[OSD([subQ30,sQuery(id+"F20.wireOp",EDGE,"E331"),sQuery(id+"F20.wireOp",EDGE,"E332")])],"isStart":true}),makeQuery(id+"F21.opExtrude","CAP_FACE",FACE,{"disambiguationData":[OSD([subQ48,sQuery(id+"F20.wireOp",EDGE,"E334"),sQuery(id+"F20.wireOp",EDGE,"E335")])],"isStart":true})]}),makeQuery(id+"F23.opExtrude","SWEPT_FACE",FACE,{"disambiguationData":[OSD([subQ50])]})]})}),makeQuery(id+"F37.opExtrude","SWEPT_FACE",FACE,{"disambiguationData":[OSD([subQ11])]})]})}),makeQuery(id+"F42.opExtrude","CAP_FACE",FACE,{"disambiguationData":[OSD([sQuery(id+"F41.wireOp",EDGE,"E374"),sQuery(id+"F41.wireOp",EDGE,"E375"),sQuery(id+"F41.wireOp",EDGE,"E376"),sQuery(id+"F41.wireOp",EDGE,"E377")])],"isStart":true})]})});}
            var sketch = newSketch(context, id + "F47", { "sketchPlane" : qUnion([Q0])});
            skLineSegment(sketch, "E390", {"start": v(-34.44, 0.43) * mm, "end": v(-34.44, -1.34) * mm});
            skLineSegment(sketch, "E391", {"start": v(-34.44, -1.34) * mm, "end": v(-35.45, -1.34) * mm});
            skLineSegment(sketch, "E392", {"start": v(-35.45, -1.34) * mm, "end": v(-35.45, 0.43) * mm});
            skLineSegment(sketch, "E393", {"start": v(-35.45, 0.43) * mm, "end": v(-34.44, 0.43) * mm});
            skSolve(sketch);
        }
        {
            var Q0;
            Q0 = qSketchRegion(id + "F47", true);
            extrude(context, id + "F48", {"entities" : qUnion([Q0]), "operationType" : NewBodyOperationType.ADD, "oppositeDirection" : true, "depth" : 25.4 * mm});
        }
        {
            var Q0;
            {var subQ11=sQuery(id+"F0.wireOp",EDGE,"E5");var subQ12=sQuery(id+"F0.wireOp",EDGE,"E1");var subQ21=makeQuery(id+"F38.opExtrude","SWEPT_FACE",FACE,{"disambiguationData":[OSD([sQuery(id+"F33.wireOp",EDGE,"E360")])]});var subQ29=sQuery(id+"F41.wireOp",EDGE,"E374");var subQ30=sQuery(id+"F41.wireOp",EDGE,"E375");var subQ31=sQuery(id+"F41.wireOp",EDGE,"E376");var subQ34=sQuery(id+"F36.wireOp",EDGE,"E367");var subQ37=sQuery(id+"F20.wireOp",EDGE,"E330");var subQ40=sQuery(id+"F0.wireOp",EDGE,"E4");var subQ41=makeQuery(id+"F1.opExtrude","SWEPT_FACE",FACE,{"disambiguationData":[OSD([subQ40])]});var subQ42=sQuery(id+"F0.wireOp",EDGE,"E3");var subQ43=sQuery(id+"F0.wireOp",EDGE,"E2");var subQ46=sQuery(id+"F20.wireOp",EDGE,"E333");var subQ48=sQuery(id+"F22.wireOp",EDGE,"E339");var subQ50=sQuery(id+"F20.wireOp",EDGE,"E327");var subQ52=sQuery(id+"F0.wireOp",EDGE,"E0");Q0=makeQuery(id+"F44.boolean.opBoolean","SPLIT",FACE,{"disambiguationData":[TD([makeQuery(id+"F38.boolean.opBoolean","COPY",FACE,{"derivedFrom":subQ21})])],"derivedFrom":makeQuery(id+"F42.boolean.opBoolean","MERGE",FACE,{"derivedFrom":[makeQuery(id+"F38.boolean.opBoolean","SPLIT",FACE,{"disambiguationData":[TD([subQ41])],"derivedFrom":makeQuery(id+"F37.boolean.opBoolean","MERGE",FACE,{"derivedFrom":[makeQuery(id+"F30.boolean.opBoolean","SPLIT",FACE,{"disambiguationData":[TD([subQ41])],"derivedFrom":makeQuery(id+"F23.boolean.opBoolean","MERGE",FACE,{"derivedFrom":[makeQuery(id+"F21.boolean.opBoolean","MERGE",FACE,{"derivedFrom":[makeQuery(id+"F1.opExtrude","CAP_FACE",FACE,{"disambiguationData":[OSD([subQ52,subQ12,subQ43,subQ42,subQ40,subQ11])],"isStart":true}),makeQuery(id+"F21.opExtrude","CAP_FACE",FACE,{"disambiguationData":[OSD([sQuery(id+"F20.wireOp",EDGE,"E324"),sQuery(id+"F20.wireOp",EDGE,"E325"),sQuery(id+"F20.wireOp",EDGE,"E326")])],"isStart":true}),makeQuery(id+"F21.opExtrude","CAP_FACE",FACE,{"disambiguationData":[OSD([subQ50,sQuery(id+"F20.wireOp",EDGE,"E328"),sQuery(id+"F20.wireOp",EDGE,"E329")])],"isStart":true}),makeQuery(id+"F21.opExtrude","CAP_FACE",FACE,{"disambiguationData":[OSD([subQ37,sQuery(id+"F20.wireOp",EDGE,"E331"),sQuery(id+"F20.wireOp",EDGE,"E332")])],"isStart":true}),makeQuery(id+"F21.opExtrude","CAP_FACE",FACE,{"disambiguationData":[OSD([subQ46,sQuery(id+"F20.wireOp",EDGE,"E334"),sQuery(id+"F20.wireOp",EDGE,"E335")])],"isStart":true})]}),makeQuery(id+"F23.opExtrude","SWEPT_FACE",FACE,{"disambiguationData":[OSD([subQ48])]})]})}),makeQuery(id+"F37.opExtrude","SWEPT_FACE",FACE,{"disambiguationData":[OSD([subQ34])]})]})}),makeQuery(id+"F42.opExtrude","CAP_FACE",FACE,{"disambiguationData":[OSD([subQ29,subQ30,subQ31,sQuery(id+"F41.wireOp",EDGE,"E377")])],"isStart":true})]})});}
            var sketch = newSketch(context, id + "F49", { "sketchPlane" : qUnion([Q0])});
            skLineSegment(sketch, "E394", {"start": v(42.78, 0.43) * mm, "end": v(42.78, -1.34) * mm});
            skLineSegment(sketch, "E395", {"start": v(42.78, -1.34) * mm, "end": v(43.8, -1.34) * mm});
            skLineSegment(sketch, "E396", {"start": v(43.8, -1.34) * mm, "end": v(43.8, 0.43) * mm});
            skLineSegment(sketch, "E397", {"start": v(43.8, 0.43) * mm, "end": v(42.78, 0.43) * mm});
            skSolve(sketch);
        }
        {
            var Q0;
            Q0 = qSketchRegion(id + "F49", true);
            extrude(context, id + "F50", {"entities" : qUnion([Q0]), "operationType" : NewBodyOperationType.ADD, "oppositeDirection" : true, "depth" : 25.4 * mm});
        }
    });
